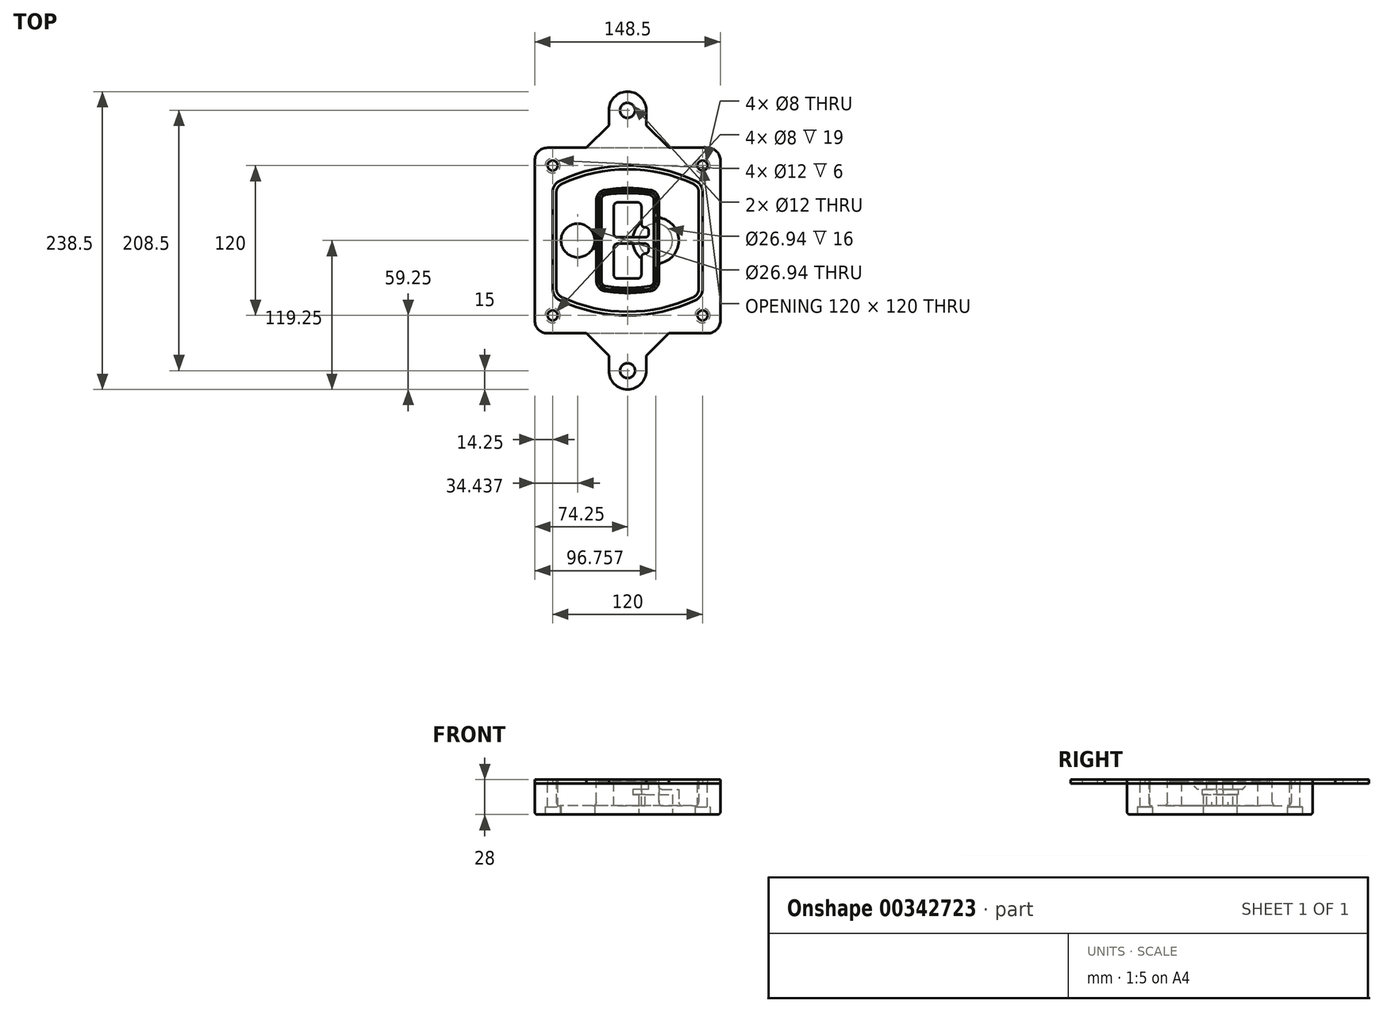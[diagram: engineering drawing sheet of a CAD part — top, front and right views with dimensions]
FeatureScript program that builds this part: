
annotation { "Feature Type Name" : "Feature", "Feature Type Description" : "" }
export const myFeature = defineFeature(function(context is Context, id is Id, definition is map)
    precondition{}
    {
        {
            var Q0;
            Q0=qCreatedBy(makeId("Top.planeOp"),FACE);
            var sketch = newSketch(context, id + "F0", { "sketchPlane" : qUnion([Q0])});
            skPoint(sketch, "E0.rect.middle", {"position": v(0, 0) * mm});
            skLineSegment(sketch, "E1.bottom", {"start": v(-64.25, -74.25) * mm, "end": v(64.25, -74.25) * mm});
            skLineSegment(sketch, "E1.top", {"start": v(-64.25, 74.25) * mm, "end": v(64.25, 74.25) * mm});
            skLineSegment(sketch, "E1.left", {"start": v(-74.25, -64.25) * mm, "end": v(-74.25, 64.25) * mm});
            skLineSegment(sketch, "E1.right", {"start": v(74.25, -64.25) * mm, "end": v(74.25, 64.25) * mm});
            skLineSegment(sketch, "E2", {"start": v(-74.25, 74.25) * mm, "end": v(74.25, -74.25) * mm, "construction": true});
            skLineSegment(sketch, "E3", {"start": v(74.25, 74.25) * mm, "end": v(-74.25, -74.25) * mm, "construction": true});
            skCircle(sketch, "E4", {"center": v(-60, 60) * mm, "radius": 4 * mm});
            skCircle(sketch, "E5", {"center": v(60, 60) * mm, "radius": 4 * mm});
            skCircle(sketch, "E6", {"center": v(60, -60) * mm, "radius": 4 * mm});
            skCircle(sketch, "E7", {"center": v(-60, -60) * mm, "radius": 4 * mm});
            skLineSegment(sketch, "E8", {"start": v(-60, 60) * mm, "end": v(60, 60) * mm, "construction": true});
            skLineSegment(sketch, "E9", {"start": v(60, 60) * mm, "end": v(60, -60) * mm, "construction": true});
            skLineSegment(sketch, "E10", {"start": v(60, -60) * mm, "end": v(-60, -60) * mm, "construction": true});
            skLineSegment(sketch, "E11", {"start": v(-60, -60) * mm, "end": v(-60, 60) * mm, "construction": true});
            skLineSegment(sketch, "E12", {"start": v(-60, 38.83) * mm, "end": v(-60, -38.83) * mm});
            skLineSegment(sketch, "E13", {"start": v(60, 38.83) * mm, "end": v(60, -38.83) * mm});
            skArc(sketch, "E14", {"start": v(54.26, 47.88) * mm, "mid": v(0, 60) * mm, "end": v(-54.26, 47.88) * mm});
            skArc(sketch, "E15", {"start": v(-54.26, -47.88) * mm, "mid": v(0, -60) * mm, "end": v(54.26, -47.88) * mm});
            skLineSegment(sketch, "E16", {"start": v(-60, 0) * mm, "end": v(60, 0) * mm, "construction": true});
            skPoint(sketch, "E17.visualSharp", {"position": v(-60, -45) * mm});
            skArc(sketch, "E17.filletArc", {"start": v(-60, -38.83) * mm, "mid": v(-58.44, -44.2) * mm, "end": v(-54.26, -47.88) * mm});
            skPoint(sketch, "E18.visualSharp", {"position": v(-60, 45) * mm});
            skArc(sketch, "E18.filletArc", {"start": v(-54.26, 47.88) * mm, "mid": v(-58.44, 44.2) * mm, "end": v(-60, 38.83) * mm});
            skPoint(sketch, "E19.visualSharp", {"position": v(60, 45) * mm});
            skArc(sketch, "E19.filletArc", {"start": v(60, 38.83) * mm, "mid": v(58.44, 44.2) * mm, "end": v(54.26, 47.88) * mm});
            skPoint(sketch, "E20.visualSharp", {"position": v(60, -45) * mm});
            skArc(sketch, "E20.filletArc", {"start": v(54.26, -47.88) * mm, "mid": v(58.44, -44.2) * mm, "end": v(60, -38.83) * mm});
            skPoint(sketch, "E21.visualSharp", {"position": v(-74.25, 74.25) * mm});
            skArc(sketch, "E21.filletArc", {"start": v(-64.25, 74.25) * mm, "mid": v(-71.32, 71.32) * mm, "end": v(-74.25, 64.25) * mm});
            skPoint(sketch, "E22.visualSharp", {"position": v(74.25, 74.25) * mm});
            skArc(sketch, "E22.filletArc", {"start": v(74.25, 64.25) * mm, "mid": v(71.32, 71.32) * mm, "end": v(64.25, 74.25) * mm});
            skPoint(sketch, "E23.visualSharp", {"position": v(74.25, -74.25) * mm});
            skArc(sketch, "E23.filletArc", {"start": v(64.25, -74.25) * mm, "mid": v(71.32, -71.32) * mm, "end": v(74.25, -64.25) * mm});
            skPoint(sketch, "E24.visualSharp", {"position": v(-74.25, -74.25) * mm});
            skArc(sketch, "E24.filletArc", {"start": v(-74.25, -64.25) * mm, "mid": v(-71.32, -71.32) * mm, "end": v(-64.25, -74.25) * mm});
            skArc(sketch, "E25.0", {"start": v(57, 38.83) * mm, "mid": v(55.9, 42.58) * mm, "end": v(52.98, 45.17) * mm});
            skLineSegment(sketch, "E25.1", {"start": v(57, 38.83) * mm, "end": v(57, -38.83) * mm});
            skArc(sketch, "E25.2", {"start": v(52.98, -45.17) * mm, "mid": v(55.9, -42.58) * mm, "end": v(57, -38.83) * mm});
            skArc(sketch, "E25.3", {"start": v(-52.98, -45.17) * mm, "mid": v(0, -57) * mm, "end": v(52.98, -45.17) * mm});
            skArc(sketch, "E25.4", {"start": v(-57, -38.83) * mm, "mid": v(-55.9, -42.58) * mm, "end": v(-52.98, -45.17) * mm});
            skArc(sketch, "E25.5", {"start": v(52.98, 45.17) * mm, "mid": v(0, 57) * mm, "end": v(-52.98, 45.17) * mm});
            skLineSegment(sketch, "E25.6", {"start": v(-57, 38.83) * mm, "end": v(-57, -38.83) * mm});
            skArc(sketch, "E25.7", {"start": v(-52.98, 45.17) * mm, "mid": v(-55.9, 42.58) * mm, "end": v(-57, 38.83) * mm});
            skArc(sketch, "E26.0", {"start": v(-55.96, 51.5) * mm, "mid": v(-61.82, 46.33) * mm, "end": v(-64, 38.83) * mm});
            skArc(sketch, "E26.1", {"start": v(55.96, 51.5) * mm, "mid": v(0, 64) * mm, "end": v(-55.96, 51.5) * mm});
            skArc(sketch, "E26.2", {"start": v(64, 38.83) * mm, "mid": v(61.82, 46.33) * mm, "end": v(55.96, 51.5) * mm});
            skLineSegment(sketch, "E26.3", {"start": v(64, 38.83) * mm, "end": v(64, -38.83) * mm});
            skArc(sketch, "E26.4", {"start": v(55.96, -51.5) * mm, "mid": v(61.82, -46.33) * mm, "end": v(64, -38.83) * mm});
            skLineSegment(sketch, "E26.5", {"start": v(-64, 38.83) * mm, "end": v(-64, -38.83) * mm});
            skArc(sketch, "E26.6", {"start": v(-55.96, -51.5) * mm, "mid": v(0, -64) * mm, "end": v(55.96, -51.5) * mm});
            skArc(sketch, "E26.7", {"start": v(-64, -38.83) * mm, "mid": v(-61.82, -46.33) * mm, "end": v(-55.96, -51.5) * mm});
            skSolve(sketch);
        }
        {
            var Q0;
            Q0=makeQuery(id+"F0.imprint","IMPRINT",FACE,{"disambiguationData":[TD([[makeQuery(id+"F0.imprint","IMPRINT",EDGE,{"derivedFrom":sQuery(id+"F0.wireOp",EDGE,"E1.bottom")}),1.0]])]});
            var Q1;
            Q1=makeQuery(id+"F0.imprint","IMPRINT",FACE,{"disambiguationData":[TD([[makeQuery(id+"F0.imprint","IMPRINT",EDGE,{"derivedFrom":sQuery(id+"F0.wireOp",EDGE,"E12")}),1.0]])]});
            var Q2;
            Q2=makeQuery(id+"F0.imprint","IMPRINT",FACE,{"disambiguationData":[TD([[makeQuery(id+"F0.imprint","IMPRINT",EDGE,{"derivedFrom":sQuery(id+"F0.wireOp",EDGE,"E25.0")}),1.0]])]});
            var Q3;
            Q3=makeQuery(id+"F0.imprint","IMPRINT",FACE,{"disambiguationData":[TD([[makeQuery(id+"F0.imprint","IMPRINT",EDGE,{"derivedFrom":sQuery(id+"F0.wireOp",EDGE,"E12")}),-1.0]])]});
            extrude(context, id + "F1", {"entities" : qUnion([Q0, Q1, Q2, Q3]), "oppositeDirection" : true, "depth" : 25 * mm});
        }
        {
            var Q0;
            Q0=makeQuery(id+"F0.imprint","IMPRINT",FACE,{"disambiguationData":[TD([[makeQuery(id+"F0.imprint","IMPRINT",EDGE,{"derivedFrom":sQuery(id+"F0.wireOp",EDGE,"E12")}),1.0]])]});
            extrude(context, id + "F2", {"entities" : qUnion([Q0]), "operationType" : NewBodyOperationType.ADD, "depth" : 3 * mm});
        }
        {
            var Q0;
            Q0=makeQuery(id+"F0.imprint","IMPRINT",FACE,{"disambiguationData":[TD([[makeQuery(id+"F0.imprint","IMPRINT",EDGE,{"derivedFrom":sQuery(id+"F0.wireOp",EDGE,"E25.0")}),1.0]])]});
            extrude(context, id + "F3", {"entities" : qUnion([Q0]), "operationType" : NewBodyOperationType.REMOVE, "oppositeDirection" : true, "depth" : 18 * mm});
        }
        {
            var Q0;
            Q0=makeQuery(id+"F2.opExtrude","CAP_FACE",FACE,{"disambiguationData":[OSD([sQuery(id+"F0.wireOp",EDGE,"E12"),sQuery(id+"F0.wireOp",EDGE,"E13"),sQuery(id+"F0.wireOp",EDGE,"E14"),sQuery(id+"F0.wireOp",EDGE,"E15"),sQuery(id+"F0.wireOp",EDGE,"E17.filletArc"),sQuery(id+"F0.wireOp",EDGE,"E18.filletArc"),sQuery(id+"F0.wireOp",EDGE,"E19.filletArc"),sQuery(id+"F0.wireOp",EDGE,"E20.filletArc"),sQuery(id+"F0.wireOp",EDGE,"E25.0"),sQuery(id+"F0.wireOp",EDGE,"E25.1"),sQuery(id+"F0.wireOp",EDGE,"E25.2"),sQuery(id+"F0.wireOp",EDGE,"E25.3"),sQuery(id+"F0.wireOp",EDGE,"E25.4"),sQuery(id+"F0.wireOp",EDGE,"E25.5"),sQuery(id+"F0.wireOp",EDGE,"E25.6"),sQuery(id+"F0.wireOp",EDGE,"E25.7")])],"isStart":false});
            var sketch = newSketch(context, id + "F4", { "sketchPlane" : qUnion([Q0])});
            skArc(sketch, "E27.0", {"start": v(-18.34, -40.45) * mm, "mid": v(0, -42) * mm, "end": v(18.34, -40.45) * mm});
            skArc(sketch, "E28.0", {"start": v(18.34, 40.45) * mm, "mid": v(0, 42) * mm, "end": v(-18.34, 40.45) * mm});
            skLineSegment(sketch, "E29", {"start": v(-25, 32.57) * mm, "end": v(-25, -32.57) * mm});
            skLineSegment(sketch, "E30", {"start": v(25, 32.57) * mm, "end": v(25, -32.57) * mm});
            skLineSegment(sketch, "E31", {"start": v(-25, 39.1) * mm, "end": v(25, 39.1) * mm, "construction": true});
            skLineSegment(sketch, "E32", {"start": v(-25, -39.1) * mm, "end": v(25, -39.1) * mm, "construction": true});
            skPoint(sketch, "E33.visualSharp", {"position": v(-25, 39.1) * mm});
            skArc(sketch, "E33.filletArc", {"start": v(-18.34, 40.45) * mm, "mid": v(-23.11, 37.73) * mm, "end": v(-25, 32.57) * mm});
            skPoint(sketch, "E34.visualSharp", {"position": v(25, 39.1) * mm});
            skArc(sketch, "E34.filletArc", {"start": v(25, 32.57) * mm, "mid": v(23.11, 37.73) * mm, "end": v(18.34, 40.45) * mm});
            skPoint(sketch, "E35.visualSharp", {"position": v(25, -39.1) * mm});
            skArc(sketch, "E35.filletArc", {"start": v(18.34, -40.45) * mm, "mid": v(23.11, -37.73) * mm, "end": v(25, -32.57) * mm});
            skPoint(sketch, "E36.visualSharp", {"position": v(-25, -39.1) * mm});
            skArc(sketch, "E36.filletArc", {"start": v(-25, -32.57) * mm, "mid": v(-23.11, -37.73) * mm, "end": v(-18.34, -40.45) * mm});
            skArc(sketch, "E37.0", {"start": v(52.98, 45.17) * mm, "mid": v(0, 57) * mm, "end": v(-52.98, 45.17) * mm});
            skArc(sketch, "E37.1", {"start": v(-52.98, 45.17) * mm, "mid": v(-55.9, 42.58) * mm, "end": v(-57, 38.83) * mm});
            skLineSegment(sketch, "E37.2", {"start": v(-57, 38.83) * mm, "end": v(-57, -38.83) * mm});
            skArc(sketch, "E37.3", {"start": v(-57, -38.83) * mm, "mid": v(-55.9, -42.58) * mm, "end": v(-52.98, -45.17) * mm});
            skArc(sketch, "E37.4", {"start": v(-52.98, -45.17) * mm, "mid": v(0, -57) * mm, "end": v(52.98, -45.17) * mm});
            skArc(sketch, "E37.5", {"start": v(52.98, -45.17) * mm, "mid": v(55.9, -42.58) * mm, "end": v(57, -38.83) * mm});
            skLineSegment(sketch, "E37.6", {"start": v(57, 38.83) * mm, "end": v(57, -38.83) * mm});
            skArc(sketch, "E37.7", {"start": v(57, 38.83) * mm, "mid": v(55.9, 42.58) * mm, "end": v(52.98, 45.17) * mm});
            skLineSegment(sketch, "E38.0", {"start": v(23, 32.57) * mm, "end": v(23, -32.57) * mm});
            skArc(sketch, "E38.1", {"start": v(18, -38.48) * mm, "mid": v(21.58, -36.44) * mm, "end": v(23, -32.57) * mm});
            skArc(sketch, "E38.2", {"start": v(-18, -38.48) * mm, "mid": v(0, -40) * mm, "end": v(18, -38.48) * mm});
            skArc(sketch, "E38.3", {"start": v(-23, -32.57) * mm, "mid": v(-21.58, -36.44) * mm, "end": v(-18, -38.48) * mm});
            skLineSegment(sketch, "E38.4", {"start": v(-23, 32.57) * mm, "end": v(-23, -32.57) * mm});
            skArc(sketch, "E38.5", {"start": v(23, 32.57) * mm, "mid": v(21.58, 36.44) * mm, "end": v(18, 38.48) * mm});
            skArc(sketch, "E38.6", {"start": v(-18, 38.48) * mm, "mid": v(-21.58, 36.44) * mm, "end": v(-23, 32.57) * mm});
            skArc(sketch, "E38.7", {"start": v(18, 38.48) * mm, "mid": v(0, 40) * mm, "end": v(-18, 38.48) * mm});
            skArc(sketch, "E39.0", {"start": v(21, 32.57) * mm, "mid": v(20.06, 35.15) * mm, "end": v(17.67, 36.5) * mm});
            skLineSegment(sketch, "E39.1", {"start": v(21, 32.57) * mm, "end": v(21, -32.57) * mm});
            skArc(sketch, "E39.2", {"start": v(17.67, -36.5) * mm, "mid": v(20.06, -35.15) * mm, "end": v(21, -32.57) * mm});
            skArc(sketch, "E39.3", {"start": v(-17.67, -36.5) * mm, "mid": v(0, -38) * mm, "end": v(17.67, -36.5) * mm});
            skArc(sketch, "E39.4", {"start": v(-21, -32.57) * mm, "mid": v(-20.06, -35.15) * mm, "end": v(-17.67, -36.5) * mm});
            skArc(sketch, "E39.5", {"start": v(17.67, 36.5) * mm, "mid": v(0, 38) * mm, "end": v(-17.67, 36.5) * mm});
            skLineSegment(sketch, "E39.6", {"start": v(-21, 32.57) * mm, "end": v(-21, -32.57) * mm});
            skArc(sketch, "E39.7", {"start": v(-17.67, 36.5) * mm, "mid": v(-20.06, 35.15) * mm, "end": v(-21, 32.57) * mm});
            skLineSegment(sketch, "E40", {"start": v(-25, 0) * mm, "end": v(25, 0) * mm, "construction": true});
            skLineSegment(sketch, "E41", {"start": v(-11, 5.5) * mm, "end": v(-11, 27.5) * mm});
            skLineSegment(sketch, "E42", {"start": v(-8, 30.5) * mm, "end": v(8, 30.5) * mm});
            skLineSegment(sketch, "E43", {"start": v(11, 27.5) * mm, "end": v(11, 13.5) * mm});
            skLineSegment(sketch, "E44", {"start": v(14, 10.5) * mm, "end": v(14, 10.5) * mm});
            skLineSegment(sketch, "E45", {"start": v(17, 7.5) * mm, "end": v(17, 5.5) * mm});
            skLineSegment(sketch, "E46", {"start": v(14, 2.5) * mm, "end": v(-8, 2.5) * mm});
            skPoint(sketch, "E47.visualSharp", {"position": v(-11, 30.5) * mm});
            skArc(sketch, "E47.filletArc", {"start": v(-8, 30.5) * mm, "mid": v(-10.12, 29.62) * mm, "end": v(-11, 27.5) * mm});
            skPoint(sketch, "E48.visualSharp", {"position": v(11, 30.5) * mm});
            skArc(sketch, "E48.filletArc", {"start": v(11, 27.5) * mm, "mid": v(10.12, 29.62) * mm, "end": v(8, 30.5) * mm});
            skPoint(sketch, "E49.visualSharp", {"position": v(11, 10.5) * mm});
            skArc(sketch, "E49.filletArc", {"start": v(11, 13.5) * mm, "mid": v(11.88, 11.38) * mm, "end": v(14, 10.5) * mm});
            skPoint(sketch, "E50.visualSharp", {"position": v(17, 10.5) * mm});
            skArc(sketch, "E50.filletArc", {"start": v(17, 7.5) * mm, "mid": v(16.12, 9.62) * mm, "end": v(14, 10.5) * mm});
            skPoint(sketch, "E51.visualSharp", {"position": v(17, 2.5) * mm});
            skArc(sketch, "E51.filletArc", {"start": v(14, 2.5) * mm, "mid": v(16.12, 3.38) * mm, "end": v(17, 5.5) * mm});
            skPoint(sketch, "E52.visualSharp", {"position": v(-11, 2.5) * mm});
            skArc(sketch, "E52.filletArc", {"start": v(-11, 5.5) * mm, "mid": v(-10.12, 3.38) * mm, "end": v(-8, 2.5) * mm});
            skLineSegment(sketch, "E53.0.MirrorCS", {"start": v(14, -2.5) * mm, "end": v(-8, -2.5) * mm});
            skArc(sketch, "E54.0.MirrorCS", {"start": v(-11, -5.5) * mm, "mid": v(-10.12, -3.38) * mm, "end": v(-8, -2.5) * mm});
            skLineSegment(sketch, "E55.0.MirrorCS", {"start": v(-11, -5.5) * mm, "end": v(-11, -27.5) * mm});
            skArc(sketch, "E56.0.MirrorCS", {"start": v(-8, -30.5) * mm, "mid": v(-10.12, -29.62) * mm, "end": v(-11, -27.5) * mm});
            skLineSegment(sketch, "E57.0.MirrorCS", {"start": v(-8, -30.5) * mm, "end": v(8, -30.5) * mm});
            skArc(sketch, "E58.0.MirrorCS", {"start": v(11, -27.5) * mm, "mid": v(10.12, -29.62) * mm, "end": v(8, -30.5) * mm});
            skLineSegment(sketch, "E59.0.MirrorCS", {"start": v(11, -27.5) * mm, "end": v(11, -13.5) * mm});
            skArc(sketch, "E60.0.MirrorCS", {"start": v(11, -13.5) * mm, "mid": v(11.88, -11.38) * mm, "end": v(14, -10.5) * mm});
            skArc(sketch, "E61.0.MirrorCS", {"start": v(17, -7.5) * mm, "mid": v(16.12, -9.62) * mm, "end": v(14, -10.5) * mm});
            skLineSegment(sketch, "E62.0.MirrorCS", {"start": v(17, -7.5) * mm, "end": v(17, -5.5) * mm});
            skArc(sketch, "E63.0.MirrorCS", {"start": v(14, -2.5) * mm, "mid": v(16.12, -3.38) * mm, "end": v(17, -5.5) * mm});
            skSolve(sketch);
        }
        {
            var Q0;
            Q0=makeQuery(id+"F4.imprint","IMPRINT",FACE,{"disambiguationData":[TD([[makeQuery(id+"F4.imprint","IMPRINT",EDGE,{"derivedFrom":sQuery(id+"F4.wireOp",EDGE,"E27.0")}),1.0]])]});
            var Q1;
            Q1=makeQuery(id+"F4.imprint","IMPRINT",FACE,{"disambiguationData":[TD([[makeQuery(id+"F4.imprint","IMPRINT",EDGE,{"derivedFrom":sQuery(id+"F4.wireOp",EDGE,"E38.0")}),-1.0]])]});
            var Q2;
            Q2=makeQuery(id+"F4.imprint","IMPRINT",FACE,{"disambiguationData":[TD([[makeQuery(id+"F4.imprint","IMPRINT",EDGE,{"derivedFrom":sQuery(id+"F4.wireOp",EDGE,"E39.0")}),1.0]])]});
            extrude(context, id + "F5", {"entities" : qUnion([Q0, Q1, Q2]), "operationType" : NewBodyOperationType.ADD, "endBound" : BoundingType.UP_TO_NEXT, "oppositeDirection" : true, "depth" : 25 * mm});
        }
        {
            var Q0;
            Q0=makeQuery(id+"F4.imprint","IMPRINT",FACE,{"disambiguationData":[TD([[makeQuery(id+"F4.imprint","IMPRINT",EDGE,{"derivedFrom":sQuery(id+"F4.wireOp",EDGE,"E38.0")}),-1.0]])]});
            extrude(context, id + "F6", {"entities" : qUnion([Q0]), "operationType" : NewBodyOperationType.REMOVE, "oppositeDirection" : true, "depth" : 2 * mm});
        }
        {
            var Q0;
            Q0=makeQuery(id+"F1.opExtrude","CAP_FACE",FACE,{"disambiguationData":[OSD([sQuery(id+"F0.wireOp",EDGE,"E1.bottom"),sQuery(id+"F0.wireOp",EDGE,"E1.top"),sQuery(id+"F0.wireOp",EDGE,"E1.left"),sQuery(id+"F0.wireOp",EDGE,"E1.right"),sQuery(id+"F0.wireOp",EDGE,"E4"),sQuery(id+"F0.wireOp",EDGE,"E5"),sQuery(id+"F0.wireOp",EDGE,"E6"),sQuery(id+"F0.wireOp",EDGE,"E7"),sQuery(id+"F0.wireOp",EDGE,"E21.filletArc"),sQuery(id+"F0.wireOp",EDGE,"E22.filletArc"),sQuery(id+"F0.wireOp",EDGE,"E23.filletArc"),sQuery(id+"F0.wireOp",EDGE,"E24.filletArc")])],"isStart":false});
            var sketch = newSketch(context, id + "F7", { "sketchPlane" : qUnion([Q0])});
            skCircle(sketch, "E64", {"center": v(22.5, 0) * mm, "radius": 13.47 * mm});
            skCircle(sketch, "E65", {"center": v(-39.81, 0) * mm, "radius": 13.47 * mm});
            skLineSegment(sketch, "E66", {"start": v(74.25, 0) * mm, "end": v(-74.25, 0) * mm});
            skCircle(sketch, "E67", {"center": v(22.5, 0) * mm, "radius": 18.47 * mm});
            skCircle(sketch, "E68", {"center": v(60, -60) * mm, "radius": 6 * mm});
            skCircle(sketch, "E69", {"center": v(-60, -60) * mm, "radius": 6 * mm});
            skCircle(sketch, "E70", {"center": v(-60, 60) * mm, "radius": 6 * mm});
            skCircle(sketch, "E71", {"center": v(60, 60) * mm, "radius": 6 * mm});
            skSolve(sketch);
        }
        {
            var Q0;
            {var subQ1=sQuery(id+"F7.wireOp",EDGE,"E66");var subQ4=sQuery(id+"F7.wireOp",EDGE,"E64");var subQ6=makeQuery(id+"F7.imprint","INTERSECT",VERTEX,{"disambiguationData":[OD(0.0)],"derivedFrom":[subQ4,subQ1]});Q0=makeQuery(id+"F7.imprint","IMPRINT",FACE,{"disambiguationData":[TD([[makeQuery(id+"F7.imprint","IMPRINT",EDGE,{"disambiguationData":[TD([[subQ6,-1.0]])],"derivedFrom":subQ4}),-1.0]])]});}
            var Q1;
            {var subQ0=sQuery(id+"F7.wireOp",EDGE,"E66");var subQ1=sQuery(id+"F7.wireOp",EDGE,"E64");var subQ3=makeQuery(id+"F7.imprint","INTERSECT",VERTEX,{"disambiguationData":[OD(0.0)],"derivedFrom":[subQ1,subQ0]});Q1=makeQuery(id+"F7.imprint","IMPRINT",FACE,{"disambiguationData":[TD([[makeQuery(id+"F7.imprint","IMPRINT",EDGE,{"disambiguationData":[TD([[subQ3,-1.0]])],"derivedFrom":subQ1}),1.0]])]});}
            var Q2;
            {var subQ0=sQuery(id+"F7.wireOp",EDGE,"E66");var subQ1=sQuery(id+"F7.wireOp",EDGE,"E64");var subQ3=makeQuery(id+"F7.imprint","INTERSECT",VERTEX,{"disambiguationData":[OD(0.0)],"derivedFrom":[subQ1,subQ0]});Q2=makeQuery(id+"F7.imprint","IMPRINT",FACE,{"disambiguationData":[TD([[makeQuery(id+"F7.imprint","IMPRINT",EDGE,{"disambiguationData":[TD([[subQ3,1.0]])],"derivedFrom":subQ1}),1.0]])]});}
            var Q3;
            {var subQ1=sQuery(id+"F7.wireOp",EDGE,"E66");var subQ4=sQuery(id+"F7.wireOp",EDGE,"E64");var subQ6=makeQuery(id+"F7.imprint","INTERSECT",VERTEX,{"disambiguationData":[OD(0.0)],"derivedFrom":[subQ4,subQ1]});Q3=makeQuery(id+"F7.imprint","IMPRINT",FACE,{"disambiguationData":[TD([[makeQuery(id+"F7.imprint","IMPRINT",EDGE,{"disambiguationData":[TD([[subQ6,1.0]])],"derivedFrom":subQ4}),-1.0]])]});}
            extrude(context, id + "F8", {"entities" : qUnion([Q0, Q1, Q2, Q3]), "operationType" : NewBodyOperationType.ADD, "oppositeDirection" : true, "depth" : 20 * mm});
        }
        {
            var Q0;
            {var subQ0=sQuery(id+"F7.wireOp",EDGE,"E66");var subQ1=sQuery(id+"F7.wireOp",EDGE,"E64");var subQ3=makeQuery(id+"F7.imprint","INTERSECT",VERTEX,{"disambiguationData":[OD(0.0)],"derivedFrom":[subQ1,subQ0]});Q0=makeQuery(id+"F7.imprint","IMPRINT",FACE,{"disambiguationData":[TD([[makeQuery(id+"F7.imprint","IMPRINT",EDGE,{"disambiguationData":[TD([[subQ3,-1.0]])],"derivedFrom":subQ1}),1.0]])]});}
            var Q1;
            {var subQ0=sQuery(id+"F7.wireOp",EDGE,"E66");var subQ1=sQuery(id+"F7.wireOp",EDGE,"E64");var subQ3=makeQuery(id+"F7.imprint","INTERSECT",VERTEX,{"disambiguationData":[OD(0.0)],"derivedFrom":[subQ1,subQ0]});Q1=makeQuery(id+"F7.imprint","IMPRINT",FACE,{"disambiguationData":[TD([[makeQuery(id+"F7.imprint","IMPRINT",EDGE,{"disambiguationData":[TD([[subQ3,1.0]])],"derivedFrom":subQ1}),1.0]])]});}
            extrude(context, id + "F9", {"entities" : qUnion([Q0, Q1]), "operationType" : NewBodyOperationType.REMOVE, "oppositeDirection" : true, "depth" : 16 * mm});
        }
        {
            var Q0;
            {var subQ0=sQuery(id+"F7.wireOp",EDGE,"E66");var subQ1=sQuery(id+"F7.wireOp",EDGE,"E65");var subQ3=makeQuery(id+"F7.imprint","INTERSECT",VERTEX,{"disambiguationData":[OD(0.0)],"derivedFrom":[subQ1,subQ0]});Q0=makeQuery(id+"F7.imprint","IMPRINT",FACE,{"disambiguationData":[TD([[makeQuery(id+"F7.imprint","IMPRINT",EDGE,{"disambiguationData":[TD([[subQ3,-1.0]])],"derivedFrom":subQ1}),1.0]])]});}
            var Q1;
            {var subQ0=sQuery(id+"F7.wireOp",EDGE,"E66");var subQ1=sQuery(id+"F7.wireOp",EDGE,"E65");var subQ3=makeQuery(id+"F7.imprint","INTERSECT",VERTEX,{"disambiguationData":[OD(0.0)],"derivedFrom":[subQ1,subQ0]});Q1=makeQuery(id+"F7.imprint","IMPRINT",FACE,{"disambiguationData":[TD([[makeQuery(id+"F7.imprint","IMPRINT",EDGE,{"disambiguationData":[TD([[subQ3,1.0]])],"derivedFrom":subQ1}),1.0]])]});}
            extrude(context, id + "F10", {"entities" : qUnion([Q0, Q1]), "operationType" : NewBodyOperationType.REMOVE, "oppositeDirection" : true, "depth" : 25 * mm});
        }
        {
            var Q0;
            Q0=makeQuery(id+"F7.imprint","IMPRINT",FACE,{"disambiguationData":[TD([[makeQuery(id+"F7.imprint","IMPRINT",EDGE,{"derivedFrom":sQuery(id+"F7.wireOp",EDGE,"E68")}),1.0]])]});
            var Q1;
            Q1=makeQuery(id+"F7.imprint","IMPRINT",FACE,{"disambiguationData":[TD([[makeQuery(id+"F7.imprint","IMPRINT",EDGE,{"derivedFrom":makeQuery(id+"F1.opExtrude","CAP_EDGE",EDGE,{"disambiguationData":[OSD([sQuery(id+"F0.wireOp",EDGE,"E5")])],"isStart":false})}),-1.0]])]});
            var Q2;
            Q2=makeQuery(id+"F7.imprint","IMPRINT",FACE,{"disambiguationData":[TD([[makeQuery(id+"F7.imprint","IMPRINT",EDGE,{"derivedFrom":sQuery(id+"F7.wireOp",EDGE,"E69")}),1.0]])]});
            var Q3;
            Q3=makeQuery(id+"F7.imprint","IMPRINT",FACE,{"disambiguationData":[TD([[makeQuery(id+"F7.imprint","IMPRINT",EDGE,{"derivedFrom":makeQuery(id+"F1.opExtrude","CAP_EDGE",EDGE,{"disambiguationData":[OSD([sQuery(id+"F0.wireOp",EDGE,"E4")])],"isStart":false})}),-1.0]])]});
            var Q4;
            Q4=makeQuery(id+"F7.imprint","IMPRINT",FACE,{"disambiguationData":[TD([[makeQuery(id+"F7.imprint","IMPRINT",EDGE,{"derivedFrom":sQuery(id+"F7.wireOp",EDGE,"E70")}),1.0]])]});
            var Q5;
            Q5=makeQuery(id+"F7.imprint","IMPRINT",FACE,{"disambiguationData":[TD([[makeQuery(id+"F7.imprint","IMPRINT",EDGE,{"derivedFrom":makeQuery(id+"F1.opExtrude","CAP_EDGE",EDGE,{"disambiguationData":[OSD([sQuery(id+"F0.wireOp",EDGE,"E7")])],"isStart":false})}),-1.0]])]});
            var Q6;
            Q6=makeQuery(id+"F7.imprint","IMPRINT",FACE,{"disambiguationData":[TD([[makeQuery(id+"F7.imprint","IMPRINT",EDGE,{"derivedFrom":sQuery(id+"F7.wireOp",EDGE,"E71")}),1.0]])]});
            var Q7;
            Q7=makeQuery(id+"F7.imprint","IMPRINT",FACE,{"disambiguationData":[TD([[makeQuery(id+"F7.imprint","IMPRINT",EDGE,{"derivedFrom":makeQuery(id+"F1.opExtrude","CAP_EDGE",EDGE,{"disambiguationData":[OSD([sQuery(id+"F0.wireOp",EDGE,"E6")])],"isStart":false})}),-1.0]])]});
            extrude(context, id + "F11", {"entities" : qUnion([Q0, Q1, Q2, Q3, Q4, Q5, Q6, Q7]), "operationType" : NewBodyOperationType.REMOVE, "oppositeDirection" : true, "depth" : 6 * mm});
        }
        {
            var Q0;
            Q0=makeQuery(id+"F9.boolean.opBoolean","COPY",FACE,{"derivedFrom":makeQuery(id+"F9.opExtrude","CAP_FACE",FACE,{"disambiguationData":[OSD([sQuery(id+"F7.wireOp",EDGE,"E64")])],"isStart":false})});
            var sketch = newSketch(context, id + "F12", { "sketchPlane" : qUnion([Q0])});
            skArc(sketch, "E72.0", {"start": v(11, 14.45) * mm, "mid": v(6.45, 9.13) * mm, "end": v(4.2, 2.5) * mm});
            skArc(sketch, "E72.1", {"start": v(4.2, -2.5) * mm, "mid": v(6.45, -9.13) * mm, "end": v(11, -14.45) * mm});
            skLineSegment(sketch, "E73", {"start": v(4.2, -2.5) * mm, "end": v(14, -2.5) * mm});
            skLineSegment(sketch, "E74.0", {"start": v(14, 2.5) * mm, "end": v(4.2, 2.5) * mm});
            skArc(sketch, "E74.1", {"start": v(14, 2.5) * mm, "mid": v(16.12, 3.38) * mm, "end": v(17, 5.5) * mm});
            skLineSegment(sketch, "E74.2", {"start": v(17, 7.5) * mm, "end": v(17, 5.5) * mm});
            skArc(sketch, "E74.3", {"start": v(17, 7.5) * mm, "mid": v(16.12, 9.62) * mm, "end": v(14, 10.5) * mm});
            skArc(sketch, "E74.4", {"start": v(11, 13.5) * mm, "mid": v(11.88, 11.38) * mm, "end": v(14, 10.5) * mm});
            skLineSegment(sketch, "E74.5", {"start": v(11, 14.45) * mm, "end": v(11, 13.5) * mm});
            skLineSegment(sketch, "E74.7", {"start": v(14, -2.5) * mm, "end": v(4.2, -2.5) * mm});
            skArc(sketch, "E74.8", {"start": v(14, -2.5) * mm, "mid": v(16.12, -3.38) * mm, "end": v(17, -5.5) * mm});
            skLineSegment(sketch, "E74.9", {"start": v(17, -7.5) * mm, "end": v(17, -5.5) * mm});
            skArc(sketch, "E74.10", {"start": v(17, -7.5) * mm, "mid": v(16.12, -9.62) * mm, "end": v(14, -10.5) * mm});
            skArc(sketch, "E74.11", {"start": v(11, -13.5) * mm, "mid": v(11.88, -11.38) * mm, "end": v(14, -10.5) * mm});
            skLineSegment(sketch, "E74.12", {"start": v(11, -14.45) * mm, "end": v(11, -13.5) * mm});
            skPoint(sketch, "E75.orphan", {"position": v(11, -27.5) * mm});
            skPoint(sketch, "E76.orphan", {"position": v(-8, -2.5) * mm});
            skPoint(sketch, "E77.orphan", {"position": v(-8, 2.5) * mm});
            skPoint(sketch, "E78.orphan", {"position": v(11, 27.5) * mm});
            skSolve(sketch);
        }
        {
            var Q0;
            {var subQ7=sQuery(id+"F12.wireOp",EDGE,"E72.0");var subQ14=sQuery(id+"F12.wireOp",EDGE,"E72.1");var subQ16=sQuery(id+"F12.wireOp",EDGE,"E74.1");var subQ18=sQuery(id+"F12.wireOp",EDGE,"E74.8");Q0=qUnion([makeQuery(id+"F12.imprint","IMPRINT",FACE,{"disambiguationData":[TD([[makeQuery(id+"F12.imprint","IMPRINT",EDGE,{"derivedFrom":subQ7}),1.0]])]}),makeQuery(id+"F12.imprint","IMPRINT",FACE,{"disambiguationData":[TD([[makeQuery(id+"F12.imprint","IMPRINT",EDGE,{"derivedFrom":subQ14}),1.0]])]}),makeQuery(id+"F12.imprint","IMPRINT",FACE,{"disambiguationData":[TD([[makeQuery(id+"F12.imprint","IMPRINT",EDGE,{"derivedFrom":subQ16}),1.0]])]}),makeQuery(id+"F12.imprint","IMPRINT",FACE,{"disambiguationData":[TD([[makeQuery(id+"F12.imprint","IMPRINT",EDGE,{"derivedFrom":subQ18}),-1.0]])]})]);}
            var Q1;
            Q1=makeQuery(id+"F5.boolean.opBoolean","SPLIT",FACE,{"disambiguationData":[TD([makeQuery(id+"F5.opExtrude","SWEPT_FACE",FACE,{"disambiguationData":[OSD([sQuery(id+"F4.wireOp",EDGE,"E41")])]})])],"derivedFrom":makeQuery(id+"F3.boolean.opBoolean","COPY",FACE,{"derivedFrom":makeQuery(id+"F3.opExtrude","CAP_FACE",FACE,{"disambiguationData":[OSD([sQuery(id+"F0.wireOp",EDGE,"E25.0"),sQuery(id+"F0.wireOp",EDGE,"E25.1"),sQuery(id+"F0.wireOp",EDGE,"E25.2"),sQuery(id+"F0.wireOp",EDGE,"E25.3"),sQuery(id+"F0.wireOp",EDGE,"E25.4"),sQuery(id+"F0.wireOp",EDGE,"E25.5"),sQuery(id+"F0.wireOp",EDGE,"E25.6"),sQuery(id+"F0.wireOp",EDGE,"E25.7")])],"isStart":false})})});
            extrude(context, id + "F13", {"entities" : qUnion([Q0]), "operationType" : NewBodyOperationType.REMOVE, "endBound" : BoundingType.UP_TO_SURFACE, "endBoundEntityFace" : qUnion([Q1]), "depth" : 25 * mm});
        }
        {
            var Q0;
            Q0=makeQuery(id+"F3.boolean.opBoolean","COPY",EDGE,{"derivedFrom":makeQuery(id+"F3.opExtrude","CAP_EDGE",EDGE,{"disambiguationData":[OSD([sQuery(id+"F0.wireOp",EDGE,"E25.6")])],"isStart":false})});
            var Q1;
            Q1=makeQuery(id+"F8.boolean.opBoolean","INTERSECT",EDGE,{"derivedFrom":[makeQuery(id+"F5.opExtrude","SWEPT_FACE",FACE,{"disambiguationData":[OSD([sQuery(id+"F4.wireOp",EDGE,"E30")])]}),makeQuery(id+"F8.opExtrude","CAP_FACE",FACE,{"disambiguationData":[OSD([sQuery(id+"F7.wireOp",EDGE,"E67")])],"isStart":false})]});
            var Q2;
            Q2=makeQuery(id+"F8.boolean.opBoolean","INTERSECT",EDGE,{"disambiguationData":[OD(1.0)],"derivedFrom":[makeQuery(id+"F5.opExtrude","SWEPT_FACE",FACE,{"disambiguationData":[OSD([sQuery(id+"F4.wireOp",EDGE,"E30")])]}),makeQuery(id+"F8.opExtrude","SWEPT_FACE",FACE,{"disambiguationData":[OSD([sQuery(id+"F7.wireOp",EDGE,"E67")])]})]});
            var Q3;
            {var subQ0=sQuery(id+"F4.wireOp",EDGE,"E30");Q3=makeQuery(id+"F8.boolean.opBoolean","SPLIT",EDGE,{"disambiguationData":[TD([makeQuery(id+"F5.opExtrude","SWEPT_FACE",FACE,{"disambiguationData":[OSD([sQuery(id+"F4.wireOp",EDGE,"E35.filletArc")])]})])],"derivedFrom":makeQuery(id+"F5.opExtrude","CAP_EDGE",EDGE,{"disambiguationData":[OSD([subQ0])],"isStart":false})});}
            var Q4;
            {var subQ0=sQuery(id+"F0.wireOp",EDGE,"E25.7");var subQ1=sQuery(id+"F0.wireOp",EDGE,"E25.1");var subQ2=sQuery(id+"F0.wireOp",EDGE,"E25.6");var subQ3=sQuery(id+"F0.wireOp",EDGE,"E25.5");var subQ4=sQuery(id+"F0.wireOp",EDGE,"E25.4");var subQ5=sQuery(id+"F0.wireOp",EDGE,"E25.0");var subQ6=sQuery(id+"F0.wireOp",EDGE,"E25.2");var subQ7=sQuery(id+"F0.wireOp",EDGE,"E25.3");Q4=makeQuery(id+"F8.boolean.opBoolean","INTERSECT",EDGE,{"derivedFrom":[makeQuery(id+"F5.boolean.opBoolean","SPLIT",FACE,{"disambiguationData":[TD([makeQuery(id+"F2.opExtrude","SWEPT_FACE",FACE,{"disambiguationData":[OSD([subQ5])]})])],"derivedFrom":makeQuery(id+"F3.boolean.opBoolean","COPY",FACE,{"derivedFrom":makeQuery(id+"F3.opExtrude","CAP_FACE",FACE,{"disambiguationData":[OSD([subQ5,subQ1,subQ6,subQ7,subQ4,subQ3,subQ2,subQ0])],"isStart":false})})}),makeQuery(id+"F8.opExtrude","SWEPT_FACE",FACE,{"disambiguationData":[OSD([sQuery(id+"F7.wireOp",EDGE,"E67")])]})]});}
            var Q5;
            Q5=makeQuery(id+"F8.boolean.opBoolean","INTERSECT",EDGE,{"disambiguationData":[OD(0.0)],"derivedFrom":[makeQuery(id+"F5.opExtrude","SWEPT_FACE",FACE,{"disambiguationData":[OSD([sQuery(id+"F4.wireOp",EDGE,"E30")])]}),makeQuery(id+"F8.opExtrude","SWEPT_FACE",FACE,{"disambiguationData":[OSD([sQuery(id+"F7.wireOp",EDGE,"E67")])]})]});
            fillet(context, id + "F14", {"entities" : qUnion([Q0, Q1, Q2, Q3, Q4, Q5]), "radius" : 3 * mm, "tangentPropagation" : true, "allowEdgeOverflow" : false});
        }
        {
            var Q0;
            Q0=makeQuery(id+"F1.opExtrude","CAP_EDGE",EDGE,{"disambiguationData":[OSD([sQuery(id+"F0.wireOp",EDGE,"E1.bottom")])],"isStart":false});
            fillet(context, id + "F15", {"entities" : qUnion([Q0]), "radius" : 2 * mm, "tangentPropagation" : true, "allowEdgeOverflow" : false});
        }
        {
            var Q0;
            {var subQ0=sQuery(id+"F0.wireOp",EDGE,"E21.filletArc");var subQ1=sQuery(id+"F0.wireOp",EDGE,"E7");var subQ2=sQuery(id+"F0.wireOp",EDGE,"E6");var subQ3=sQuery(id+"F0.wireOp",EDGE,"E5");var subQ4=sQuery(id+"F0.wireOp",EDGE,"E4");var subQ5=sQuery(id+"F0.wireOp",EDGE,"E22.filletArc");var subQ6=sQuery(id+"F0.wireOp",EDGE,"E1.bottom");var subQ7=sQuery(id+"F0.wireOp",EDGE,"E1.right");var subQ8=sQuery(id+"F0.wireOp",EDGE,"E1.top");var subQ9=sQuery(id+"F0.wireOp",EDGE,"E1.left");var subQ10=sQuery(id+"F0.wireOp",EDGE,"E23.filletArc");var subQ11=sQuery(id+"F0.wireOp",EDGE,"E24.filletArc");Q0=makeQuery(id+"F2.boolean.opBoolean","SPLIT",FACE,{"disambiguationData":[TD([makeQuery(id+"F1.opExtrude","SWEPT_FACE",FACE,{"disambiguationData":[OSD([subQ6])]})])],"derivedFrom":makeQuery(id+"F1.opExtrude","CAP_FACE",FACE,{"disambiguationData":[OSD([subQ6,subQ8,subQ9,subQ7,subQ4,subQ3,subQ2,subQ1,subQ0,subQ5,subQ10,subQ11])],"isStart":true})});}
            var sketch = newSketch(context, id + "F16", { "sketchPlane" : qUnion([Q0])});
            skLineSegment(sketch, "E79.0", {"start": v(-64.25, 74.25) * mm, "end": v(64.25, 74.25) * mm});
            skArc(sketch, "E79.1", {"start": v(-64.25, 74.25) * mm, "mid": v(-71.32, 71.32) * mm, "end": v(-74.25, 64.25) * mm});
            skLineSegment(sketch, "E79.2", {"start": v(-74.25, -64.25) * mm, "end": v(-74.25, 64.25) * mm});
            skArc(sketch, "E79.3", {"start": v(-74.25, -64.25) * mm, "mid": v(-71.32, -71.32) * mm, "end": v(-64.25, -74.25) * mm});
            skLineSegment(sketch, "E79.4", {"start": v(-64.25, -74.25) * mm, "end": v(64.25, -74.25) * mm});
            skArc(sketch, "E79.5", {"start": v(64.25, -74.25) * mm, "mid": v(71.32, -71.32) * mm, "end": v(74.25, -64.25) * mm});
            skLineSegment(sketch, "E79.6", {"start": v(74.25, -64.25) * mm, "end": v(74.25, 64.25) * mm});
            skArc(sketch, "E79.7", {"start": v(74.25, 64.25) * mm, "mid": v(71.32, 71.32) * mm, "end": v(64.25, 74.25) * mm});
            skLineSegment(sketch, "E80", {"start": v(-33, 74.25) * mm, "end": v(-15, 92.25) * mm});
            skLineSegment(sketch, "E81", {"start": v(-15, 92.25) * mm, "end": v(-15, 104.25) * mm});
            skLineSegment(sketch, "E82", {"start": v(33, 74.25) * mm, "end": v(15, 92.25) * mm});
            skLineSegment(sketch, "E83", {"start": v(15, 92.25) * mm, "end": v(15, 104.25) * mm});
            skArc(sketch, "E84", {"start": v(15, 104.25) * mm, "mid": v(0, 119.25) * mm, "end": v(-15, 104.25) * mm});
            skCircle(sketch, "E85", {"center": v(0, 104.25) * mm, "radius": 6 * mm});
            skLineSegment(sketch, "E86", {"start": v(0, 104.25) * mm, "end": v(0, 74.25) * mm, "construction": true});
            skLineSegment(sketch, "E87", {"start": v(-74.25, 0) * mm, "end": v(74.25, 0) * mm, "construction": true});
            skLineSegment(sketch, "E88.MirrorCS", {"start": v(-33, -74.25) * mm, "end": v(-15, -92.25) * mm});
            skLineSegment(sketch, "E89.MirrorCS", {"start": v(-15, -92.25) * mm, "end": v(-15, -104.25) * mm});
            skArc(sketch, "E90.MirrorCS", {"start": v(15, -104.25) * mm, "mid": v(0, -119.25) * mm, "end": v(-15, -104.25) * mm});
            skLineSegment(sketch, "E91.MirrorCS", {"start": v(15, -92.25) * mm, "end": v(15, -104.25) * mm});
            skCircle(sketch, "E92.MirrorC", {"center": v(0, -104.25) * mm, "radius": 6 * mm});
            skLineSegment(sketch, "E93.MirrorCS", {"start": v(0, -104.25) * mm, "end": v(0, -74.25) * mm, "construction": true});
            skLineSegment(sketch, "E94.MirrorCS", {"start": v(33, -74.25) * mm, "end": v(15, -92.25) * mm});
            skSolve(sketch);
        }
        {
            var Q0;
            {var subQ1=sQuery(id+"F16.wireOp",EDGE,"E80");Q0=makeQuery(id+"F16.imprint","IMPRINT",FACE,{"disambiguationData":[TD([[makeQuery(id+"F16.imprint","IMPRINT",EDGE,{"derivedFrom":subQ1}),-1.0]])]});}
            var Q1;
            {var subQ1=sQuery(id+"F16.wireOp",EDGE,"E79.1");Q1=makeQuery(id+"F16.imprint","IMPRINT",FACE,{"disambiguationData":[TD([[makeQuery(id+"F16.imprint","IMPRINT",EDGE,{"derivedFrom":subQ1}),1.0]])]});}
            var Q2;
            {var subQ0=sQuery(id+"F16.wireOp",EDGE,"E88.MirrorCS");Q2=makeQuery(id+"F16.imprint","IMPRINT",FACE,{"disambiguationData":[TD([[makeQuery(id+"F16.imprint","IMPRINT",EDGE,{"derivedFrom":subQ0}),1.0]])]});}
            var Q3;
            Q3=makeQuery(id+"F2.opExtrude","CAP_FACE",FACE,{"disambiguationData":[OSD([sQuery(id+"F0.wireOp",EDGE,"E12"),sQuery(id+"F0.wireOp",EDGE,"E13"),sQuery(id+"F0.wireOp",EDGE,"E14"),sQuery(id+"F0.wireOp",EDGE,"E15"),sQuery(id+"F0.wireOp",EDGE,"E17.filletArc"),sQuery(id+"F0.wireOp",EDGE,"E18.filletArc"),sQuery(id+"F0.wireOp",EDGE,"E19.filletArc"),sQuery(id+"F0.wireOp",EDGE,"E20.filletArc"),sQuery(id+"F0.wireOp",EDGE,"E25.0"),sQuery(id+"F0.wireOp",EDGE,"E25.1"),sQuery(id+"F0.wireOp",EDGE,"E25.2"),sQuery(id+"F0.wireOp",EDGE,"E25.3"),sQuery(id+"F0.wireOp",EDGE,"E25.4"),sQuery(id+"F0.wireOp",EDGE,"E25.5"),sQuery(id+"F0.wireOp",EDGE,"E25.6"),sQuery(id+"F0.wireOp",EDGE,"E25.7")])],"isStart":false});
            extrude(context, id + "F17", {"entities" : qUnion([Q0, Q1, Q2]), "endBound" : BoundingType.UP_TO_SURFACE, "endBoundEntityFace" : qUnion([Q3]), "depth" : 25 * mm});
        }
    });
